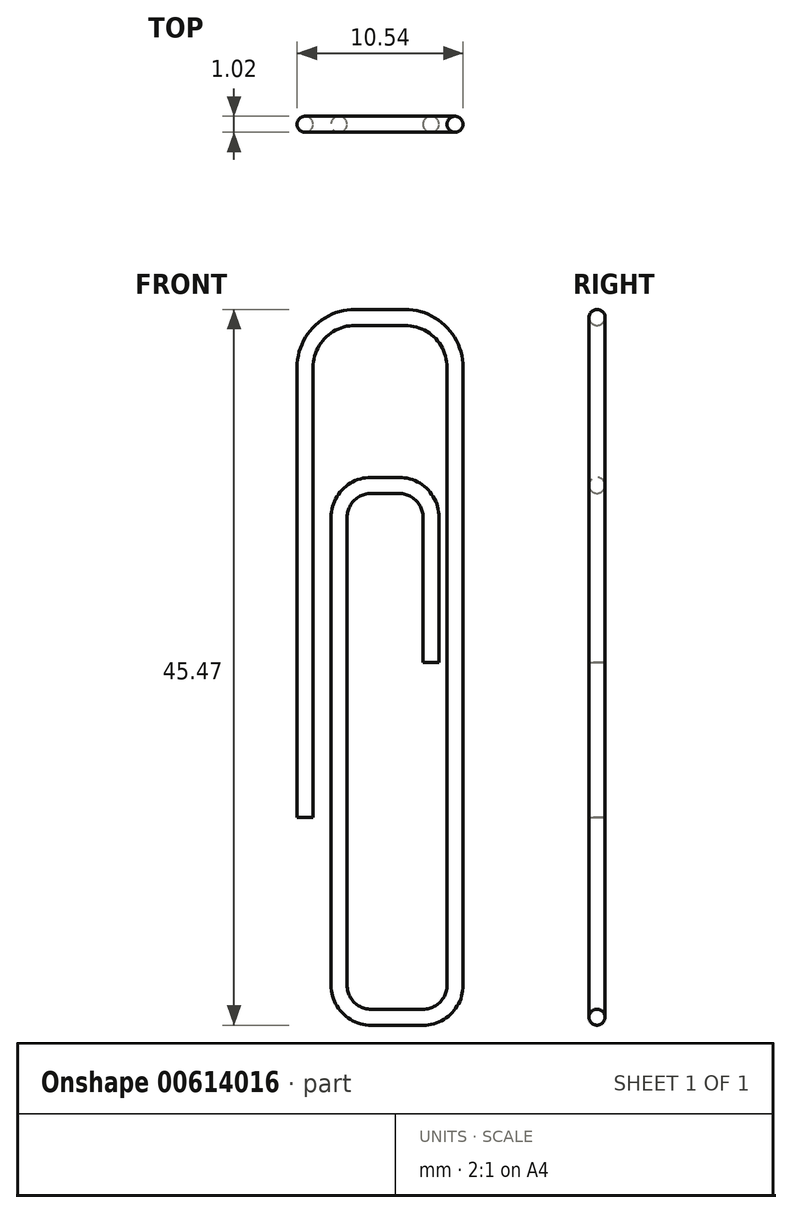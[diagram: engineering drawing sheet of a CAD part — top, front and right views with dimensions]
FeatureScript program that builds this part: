
annotation { "Feature Type Name" : "Feature", "Feature Type Description" : "" }
export const myFeature = defineFeature(function(context is Context, id is Id, definition is map)
    precondition{}
    {
        {
            var Q0;
            Q0=qCreatedBy(makeId("Front.planeOp"),FACE);
            var sketch = newSketch(context, id + "F0", { "sketchPlane" : qUnion([Q0])});
            skLineSegment(sketch, "E0", {"start": v(0, 2.03) * mm, "end": v(0, 38.1) * mm});
            skLineSegment(sketch, "E1", {"start": v(-9.52, 41.28) * mm, "end": v(-9.52, 12.7) * mm});
            skLineSegment(sketch, "E2", {"start": v(0, 38.1) * mm, "end": v(0, 41.28) * mm});
            skLineSegment(sketch, "E3", {"start": v(-6.35, 44.45) * mm, "end": v(-3.17, 44.45) * mm});
            skPoint(sketch, "E4.visualSharp", {"position": v(0, 44.45) * mm});
            skArc(sketch, "E4.filletArc", {"start": v(0, 41.28) * mm, "mid": v(-0.93, 43.52) * mm, "end": v(-3.17, 44.45) * mm});
            skArc(sketch, "E5.filletArc", {"start": v(-6.35, 44.45) * mm, "mid": v(-8.6, 43.52) * mm, "end": v(-9.52, 41.28) * mm});
            skLineSegment(sketch, "E6", {"start": v(-7.37, 2.03) * mm, "end": v(-7.37, 31.75) * mm});
            skPoint(sketch, "E7.visualSharp", {"position": v(-7.37, 0) * mm});
            skArc(sketch, "E7.filletArc", {"start": v(-7.37, 2.03) * mm, "mid": v(-6.77, 0.6) * mm, "end": v(-5.33, 0) * mm});
            skLineSegment(sketch, "E8", {"start": v(-2.03, 0) * mm, "end": v(-5.33, 0) * mm});
            skPoint(sketch, "E9.visualSharp", {"position": v(0, 0) * mm});
            skArc(sketch, "E9.filletArc", {"start": v(-2.03, 0) * mm, "mid": v(-0.6, 0.6) * mm, "end": v(0, 2.03) * mm});
            skLineSegment(sketch, "E10", {"start": v(-1.52, 30.48) * mm, "end": v(-1.52, 22.54) * mm});
            skPoint(sketch, "E11.visualSharp", {"position": v(-7.37, 33.78) * mm});
            skArc(sketch, "E11.filletArc", {"start": v(-5.33, 33.78) * mm, "mid": v(-6.77, 33.19) * mm, "end": v(-7.37, 31.75) * mm});
            skLineSegment(sketch, "E12", {"start": v(-1.52, 30.48) * mm, "end": v(-1.52, 31.75) * mm});
            skPoint(sketch, "E12.endSnap0", {"position": v(-3.43, 33.78) * mm});
            skLineSegment(sketch, "E13", {"start": v(-3.56, 33.78) * mm, "end": v(-5.33, 33.78) * mm});
            skPoint(sketch, "E14.visualSharp", {"position": v(-1.52, 33.78) * mm});
            skArc(sketch, "E14.filletArc", {"start": v(-1.52, 31.75) * mm, "mid": v(-2.12, 33.19) * mm, "end": v(-3.56, 33.78) * mm});
            skSolve(sketch);
        }
        {
            var Q0;
            Q0=qCreatedBy(makeId("Top.planeOp"),FACE);
            var Q1;
            Q1=sQuery(id+"F0.wireOp",VERTEX,"E1.end");
            cPlane(context, id + "F1", {"entities" : qUnion([Q0, Q1]), "cplaneType" : CPlaneType.PLANE_POINT, "offset" : 25.4 * mm, "width" : 152.4 * mm, "height" : 152.4 * mm});
        }
        {
            var Q0;
            Q0=qCreatedBy(id+"F1.planeOp",FACE);
            var sketch = newSketch(context, id + "F2", { "sketchPlane" : qUnion([Q0])});
            skPoint(sketch, "E15.0", {"position": v(-9.52, 0) * mm});
            skCircle(sketch, "E16", {"center": v(-9.52, 0) * mm, "radius": 0.5 * mm});
            skSolve(sketch);
        }
        {
            var Q0;
            Q0=makeQuery(id+"F2.imprint","IMPRINT",FACE,{"disambiguationData":[TD([[makeQuery(id+"F2.imprint","IMPRINT",EDGE,{"derivedFrom":sQuery(id+"F2.wireOp",EDGE,"E16")}),1.0]])]});
            var Q1;
            Q1=sQuery(id+"F0.wireOp",EDGE,"E11.filletArc");
            var Q2;
            Q2=sQuery(id+"F0.wireOp",EDGE,"E13");
            var Q3;
            Q3=sQuery(id+"F0.wireOp",EDGE,"E14.filletArc");
            var Q4;
            Q4=sQuery(id+"F0.wireOp",EDGE,"E1");
            var Q5;
            Q5=sQuery(id+"F0.wireOp",EDGE,"E5.filletArc");
            var Q6;
            Q6=sQuery(id+"F0.wireOp",EDGE,"E3");
            var Q7;
            Q7=sQuery(id+"F0.wireOp",EDGE,"E4.filletArc");
            var Q8;
            Q8=sQuery(id+"F0.wireOp",EDGE,"E2");
            var Q9;
            Q9=sQuery(id+"F0.wireOp",EDGE,"E0");
            var Q10;
            Q10=sQuery(id+"F0.wireOp",EDGE,"E9.filletArc");
            var Q11;
            Q11=sQuery(id+"F0.wireOp",EDGE,"E8");
            var Q12;
            Q12=sQuery(id+"F0.wireOp",EDGE,"E7.filletArc");
            var Q13;
            Q13=sQuery(id+"F0.wireOp",EDGE,"E6");
            var Q14;
            Q14=sQuery(id+"F0.wireOp",EDGE,"E12");
            var Q15;
            Q15=sQuery(id+"F0.wireOp",EDGE,"E10");
            sweep(context, id + "F3", {"profiles" : qUnion([Q0]), "path" : qUnion([Q1, Q2, Q3, Q4, Q5, Q6, Q7, Q8, Q9, Q10, Q11, Q12, Q13, Q14, Q15])});
        }
    });
